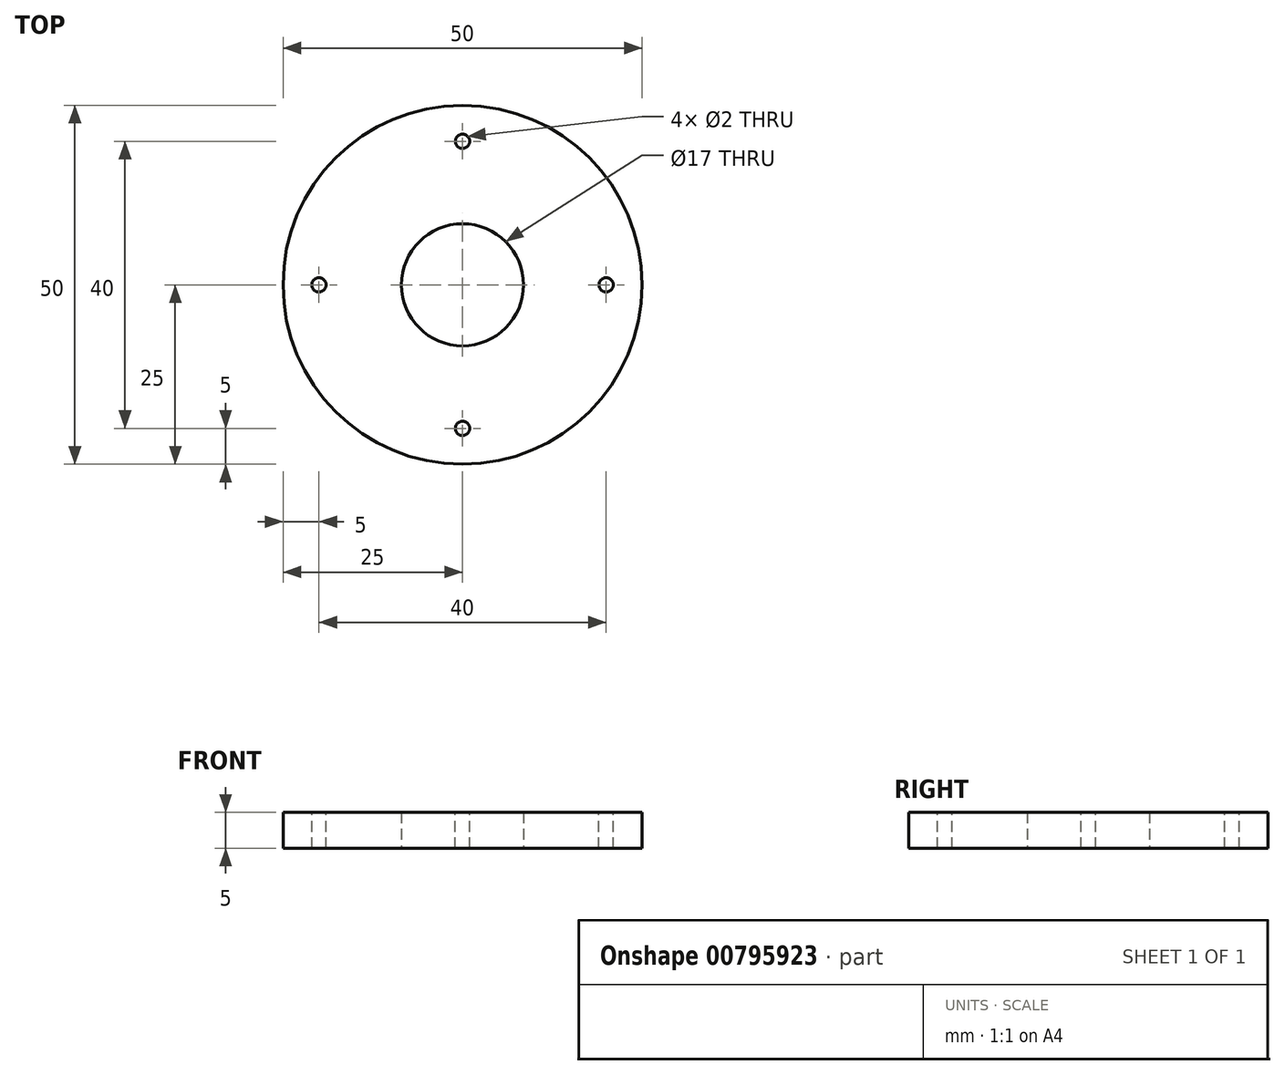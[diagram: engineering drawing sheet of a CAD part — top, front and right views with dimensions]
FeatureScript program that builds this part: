
annotation { "Feature Type Name" : "Feature", "Feature Type Description" : "" }
export const myFeature = defineFeature(function(context is Context, id is Id, definition is map)
    precondition{}
    {
        {
            var Q0;
            Q0=qCreatedBy(makeId("Top.planeOp"),FACE);
            var sketch = newSketch(context, id + "F0", { "sketchPlane" : qUnion([Q0])});
            skCircle(sketch, "E0", {"center": v(0, 0) * mm, "radius": 25 * mm});
            skCircle(sketch, "E1", {"center": v(0, 0) * mm, "radius": 8.5 * mm});
            skSolve(sketch);
        }
        {
            var Q0;
            Q0 = qSketchRegion(id + "F0", true);
            extrude(context, id + "F1", {"entities" : qUnion([Q0]), "depth" : 5 * mm, "offsetDistance" : 25 * mm});
        }
        {
            var Q0;
            Q0=makeQuery(id+"F1.opExtrude","CAP_FACE",FACE,{"disambiguationData":[OSD([sQuery(id+"F0.wireOp",EDGE,"E0"),sQuery(id+"F0.wireOp",EDGE,"E1")])],"isStart":false});
            var sketch = newSketch(context, id + "F2", { "sketchPlane" : qUnion([Q0])});
            skLineSegment(sketch, "E2", {"start": v(0, 25) * mm, "end": v(0, -25) * mm, "construction": true});
            skCircle(sketch, "E3", {"center": v(0, 20) * mm, "radius": 1 * mm});
            skCircle(sketch, "E4.1.0", {"center": v(-20, 0) * mm, "radius": 1 * mm});
            skCircle(sketch, "E4.2.0", {"center": v(0, -20) * mm, "radius": 1 * mm});
            skCircle(sketch, "E4.3.0", {"center": v(20, 0) * mm, "radius": 1 * mm});
            skPoint(sketch, "E4.center", {"position": v(0, 0) * mm});
            skSolve(sketch);
        }
        {
            var Q0;
            Q0 = qSketchRegion(id + "F2", true);
            var Q1;
            Q1 = qConstructionFilter(qBodyType(qCreatedBy(id + "F2" ,EDGE), BodyType.WIRE), ConstructionObject.NO);
            extrude(context, id + "F3", {"entities" : qUnion([Q0]), "operationType" : NewBodyOperationType.REMOVE, "surfaceEntities" : qUnion([Q1]), "endBound" : BoundingType.THROUGH_ALL, "oppositeDirection" : true, "depth" : 25 * mm, "offsetDistance" : 25 * mm});
        }
    });
